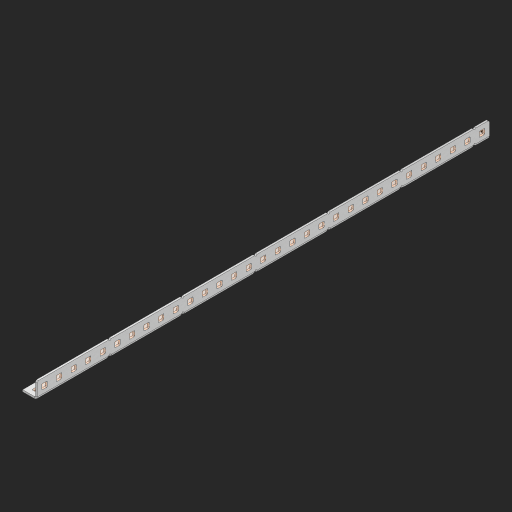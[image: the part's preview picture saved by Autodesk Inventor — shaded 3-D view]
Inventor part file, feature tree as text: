
AUTODESK INVENTOR PART (.ipt)
format: ipt  version: 2023 (Build 270158000, 158)  size: 983,040 bytes
history: native  units: in
note: dims shown in document units (in); Inventor stores cm internally (conversion verified against a paired STEP export)
features: other x67, extrude x61, sheet_metal_op x10, sketch x8, mirror x1, pattern_linear x1, chamfer x1
ambient origin geometry x8: Origin, YZ Plane, XZ Plane, XY Plane, X Axis, Y Axis, Z Axis, Center Point
bodies: Solid1 (feature_tree), Body (feature_tree)
feature tree (149):
  other  "Flange Pattern Plane"
  sheet_metal_op  "Flange Pattern"
  sheet_metal_op  "Body Pattern"
  other  "Arc Length"
  mirror  "Notch Mirror"
  pattern_linear  "Notch Pattern"  Spacing1=0.25in  [1 undecoded]
  chamfer  "End Chamfer"
  extrude  "Half Cut"  Depth=0.0625in
  sketch  "Sketch1"  dims[d0=1.5in]
  other  "Plate1"
  sketch  "Sketch2"  dims[d1=15.5in]
  other  "Plate2"
  sheet_metal_op  "Bend1"
  sheet_metal_op  "Corner1"
  sketch  "Sketch3"  dims[d2=0.0625in]
  other  "Flange Pattern Sketch"
  sketch  "Sketch7"  dims[d3=0.0625in]
  other  "Srf1"
  other  "Srf2"
  sketch  "Sketch8"  dims[d4=0.0312in]
  sketch  "Sketch9"  dims[d5=0.125in]
  other  "Srf91"
  sheet_metal_op  "Body Pattern Sketch"
  other  "Srf92"
  sketch  "Sketch13"  dims[d6=0.0625in]
  sketch  "Sketch14"  dims[d7=0.5in d8=90.0deg d9=0.0312in d10=0.25in d11=0.0625in d12=0.0625in d16=0.182in d17=0.02in d18=0.0625in d19=0.0in d20=0.25in d21=0.25in d46=0.172in d47=1.0in d48=0.0in d49=0.182in d50=0.02in d51=0.25in d52=0.25in d53=0.0625in d54=0.0in d55=0.172in d56=1.0in d57=0.0in d60=12.2047in d62=0.5in d63=0.3937in d65=0.5in d85=0.1473in d86=0.1782in d88=0.04in d89=0.0625in d90=0.0in d91=0.04in d92=0.0491in d95=2.5in d96=0.04in d97=0.25in d98=45.0deg d101=0.0in d102=2.497in d131=0.5in d132=12.2047in d134=0.5in d139=0.5in]
  other  "Srf856"
  other  "Srf1310"
  other  "Srf1311"
  other  "Srf1312"
  other  "Srf1376"
  other  "Srf1377"
  other  "Srf1728"
  other  "Srf1755"
  other  "Srf1878"
  other  "Srf1879"
  other  "Srf1880"
  other  "Srf1881"
  other  "Srf1882"
  other  "Srf1883"
  other  "Srf1884"
  other  "Srf1885"
  other  "Srf1886"
  other  "Srf1887"
  other  "Srf1888"
  other  "Srf1889"
  other  "Srf1890"
  other  "Srf1891"
  other  "Srf1892"
  other  "Srf1893"
  other  "Srf1894"
  other  "Srf1895"
  other  "Srf1896"
  other  "Srf1897"
  other  "Srf1898"
  other  "Srf1899"
  other  "Srf1900"
  other  "Srf1901"
  other  "Srf1902"
  other  "Srf1942"
  other  "Srf1943"
  other  "Srf1944"
  other  "Srf1945"
  other  "Srf1946"
  other  "Srf1947"
  other  "Srf1948"
  other  "Srf1949"
  other  "Srf1950"
  other  "Srf1951"
  other  "Srf1952"
  other  "Srf1953"
  other  "Srf1954"
  other  "Srf1955"
  other  "Srf1956"
  other  "Srf1957"
  other  "Srf1958"
  other  "Srf1959"
  other  "Srf1960"
  other  "Srf1961"
  other  "Srf1962"
  other  "Srf1963"
  other  "Srf1964"
  other  "Srf1965"
  other  "Srf1966"
  sheet_metal_op  "Flange Stamp"
  sheet_metal_op  "Flange Circle"
  sheet_metal_op  "Body Stamp"
  sheet_metal_op  "Body Circle"
  sheet_metal_op  "Notch"
  extrude  "ExtrusionSrf2"  Depth=0.0625in
  extrude  "ExtrusionSrf92"  Depth=0.5in
  extrude  "ExtrusionSrf856"  Depth=0.02in
  extrude  "ExtrusionSrf1310"  Depth=0.0625in
  extrude  "ExtrusionSrf1311"  TaperAngle=0.0deg  [1 undecoded]
  extrude  "ExtrusionSrf1312"  Depth=0.5in
  extrude  "ExtrusionSrf1376"  Depth=0.5in
  extrude  "ExtrusionSrf1377"  Depth=0.5in
  extrude  "ExtrusionSrf1728"  Depth=0.5in TaperAngle=0.0deg
  extrude  "ExtrusionSrf1755"  Depth=0.5in
  extrude  "ExtrusionSrf1878"  Depth=0.02in
  extrude  "ExtrusionSrf1879"  Depth=0.5in
  extrude  "ExtrusionSrf1880"  Depth=0.5in
  extrude  "ExtrusionSrf1881"  Depth=0.0625in
  extrude  "ExtrusionSrf1882"  TaperAngle=0.0deg  [1 undecoded]
  extrude  "ExtrusionSrf1883"  Depth=0.5in
  extrude  "ExtrusionSrf1884"  Depth=0.5in TaperAngle=0.0deg
  extrude  "ExtrusionSrf1885"  Depth=0.5in
  extrude  "ExtrusionSrf1886"  Depth=0.5in
  extrude  "ExtrusionSrf1887"  Depth=0.5in
  extrude  "ExtrusionSrf1888"  Depth=0.5in
  extrude  "ExtrusionSrf1889"  Depth=0.5in
  extrude  "ExtrusionSrf1890"  Depth=0.0625in
  extrude  "ExtrusionSrf1891"  TaperAngle=0.0deg  [1 undecoded]
  extrude  "ExtrusionSrf1892"  Depth=0.5in
  extrude  "ExtrusionSrf1893"  Depth=0.5in
  extrude  "ExtrusionSrf1894"  Depth=0.5in
  extrude  "ExtrusionSrf1895"  Depth=0.5in TaperAngle=45.0deg
  extrude  "ExtrusionSrf1896"  TaperAngle=0.0deg  [1 undecoded]
  extrude  "ExtrusionSrf1897"  Depth=0.5in
  extrude  "ExtrusionSrf1898"  Depth=0.5in
  extrude  "ExtrusionSrf1899"  Depth=0.5in
  extrude  "ExtrusionSrf1900"  Depth=0.5in
  extrude  "ExtrusionSrf1901"  Depth=0.5in
  extrude  "ExtrusionSrf1902"  [1 undecoded]
  extrude  "ExtrusionSrf1942"  [1 undecoded]
  extrude  "ExtrusionSrf1943"  [1 undecoded]
  extrude  "ExtrusionSrf1944"  [1 undecoded]
  extrude  "ExtrusionSrf1945"  [1 undecoded]
  extrude  "ExtrusionSrf1946"  [1 undecoded]
  extrude  "ExtrusionSrf1947"  [1 undecoded]
  extrude  "ExtrusionSrf1948"  [1 undecoded]
  extrude  "ExtrusionSrf1949"  [1 undecoded]
  extrude  "ExtrusionSrf1950"  [1 undecoded]
  extrude  "ExtrusionSrf1951"  [1 undecoded]
  extrude  "ExtrusionSrf1952"  [1 undecoded]
  extrude  "ExtrusionSrf1953"  [1 undecoded]
  extrude  "ExtrusionSrf1954"  [1 undecoded]
  extrude  "ExtrusionSrf1955"  [1 undecoded]
  extrude  "ExtrusionSrf1956"  [1 undecoded]
  extrude  "ExtrusionSrf1957"  [1 undecoded]
  extrude  "ExtrusionSrf1958"  [1 undecoded]
  extrude  "ExtrusionSrf1959"  [1 undecoded]
  extrude  "ExtrusionSrf1960"  [1 undecoded]
  extrude  "ExtrusionSrf1961"  [1 undecoded]
  extrude  "ExtrusionSrf1962"  [1 undecoded]
  extrude  "ExtrusionSrf1963"  [1 undecoded]
  extrude  "ExtrusionSrf1964"  [1 undecoded]
  extrude  "ExtrusionSrf1965"  [1 undecoded]
  extrude  "ExtrusionSrf1966"  [1 undecoded]
note: 31 required parameter values undecoded (feature->parameter linkage not recoverable at this tier; creation-order binding heuristic only, values carry confidence <= 0.55)
